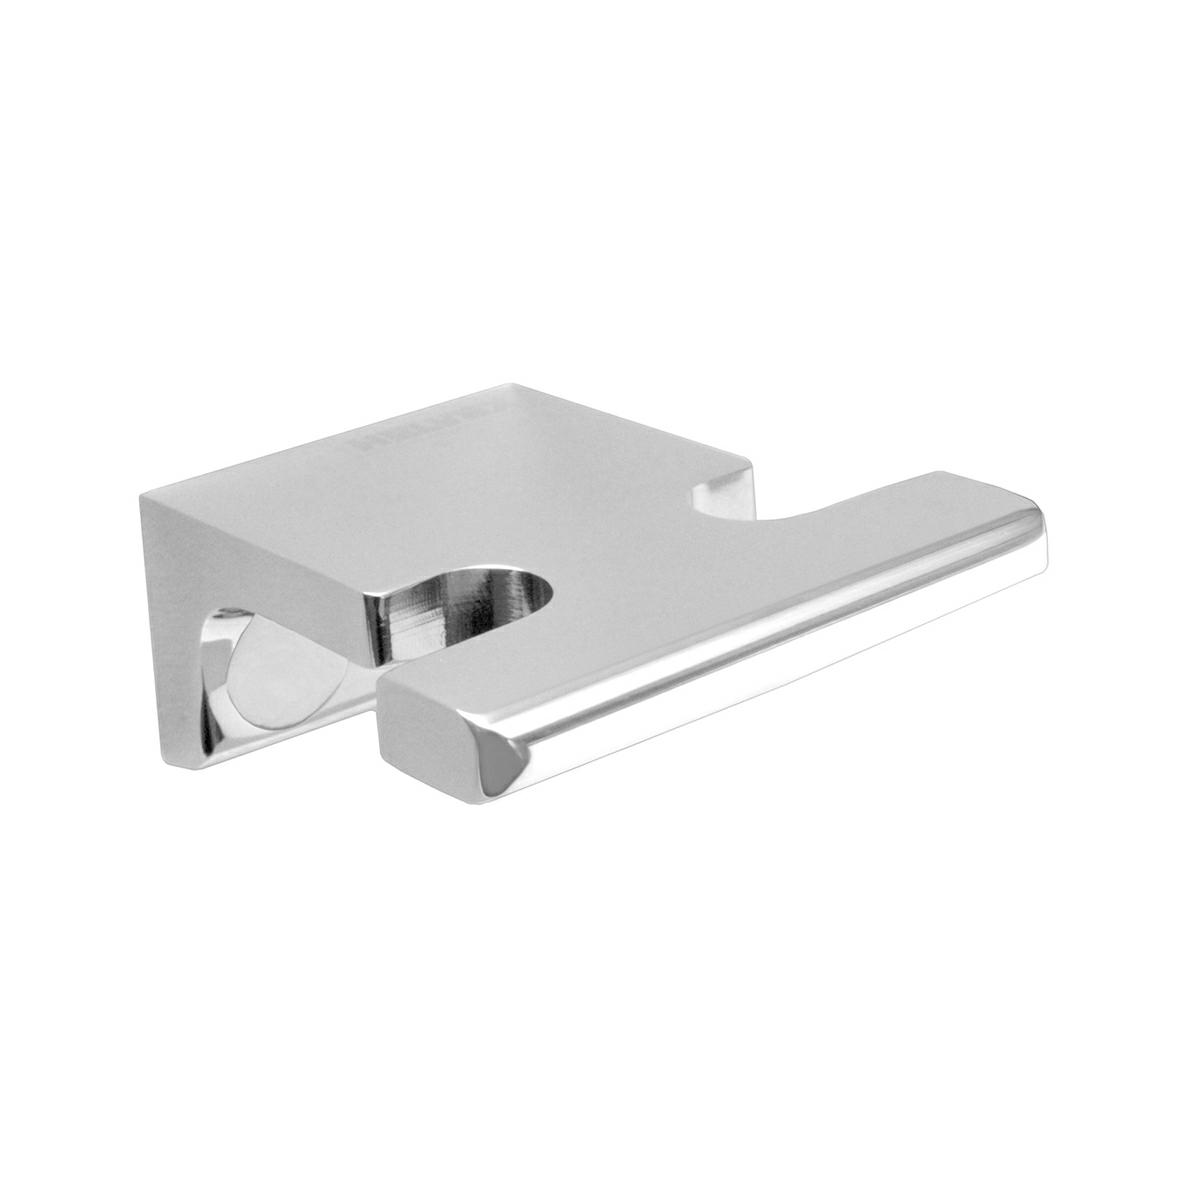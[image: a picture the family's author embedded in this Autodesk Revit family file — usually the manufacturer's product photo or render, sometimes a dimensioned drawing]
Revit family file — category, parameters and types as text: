
# Revit family: ACC-106
name_source: partatom
category: Aparatos sanitarios
units: mm (PartAtom-declared; Revit-internal decimal feet)

## family parameters
Compartido = No
Corte con vacíos al cargar = No
Cota de conector redondo = Diámetro de uso
Número OmniClass = 23.45.00.00
Punto de cálculo de habitación = No
Se basa en plano de trabajo = No
Siempre vertical = Sí
Tipo de pieza = Normal
Título OmniClass = Sanitary, Laundry, and Cleaning Equipment

## types (3) — shared parameters
Brass Chromed = Brass
Comentarios de tipo = Accesories
Elevación por defecto = 0"
Fabricante = HELVEX
Total Depth = 3"

## per-type parameters (varying)
| type | Data Sheet | Descripción | Features | Imagen de tipo | Instructive | Total Length | Total Support Diameter | URL | Ébano |
| 14104 | http://helvex.com | Kúbica Paper Holder | Wall Mounted Accessory; Setting Kit Included; Includes Fastening Tool | <Ninguno> | http://helvex.com | 8" | 2" | http://helvex.com | <Por categoría> |
| ACC-105 | https://www.helvex.com.mx | Toallero de barra Access | Bar towel rack Accessed. | <Ninguno> | https://www.helvex.com.mx | 24" | 1" | https://www.helvex.com.mx | <Por categoría> |
| ACC-106 | https://www.helvex.com.mx | Gancho sencillo Access | Access simple hook | ACC-106.jpg | https://www.helvex.com.mx | 2" | 1" | https://www.helvex.com.mx | Ébano |

note: column(s) folded — value = type name in every type: Modelo

## geometry (parser evidence)
native form markers: Sweep x3
no freeform markers — native parametric forms only
